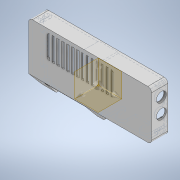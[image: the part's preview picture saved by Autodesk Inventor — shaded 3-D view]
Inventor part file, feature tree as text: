
AUTODESK INVENTOR PART (.ipt)
format: ipt  version: 2021 (Build 250183000, 183)  size: 576,512 bytes
history: native  units: mm
features: sketch x23, extrude x22, chamfer x6, fillet x5, hole x1
ambient origin geometry x8: Origin, YZ Plane, XZ Plane, XY Plane, X Axis, Y Axis, Z Axis, Center Point
bodies: Solid1 (feature_tree)
feature tree (57):
  extrude  "Extrusion1"  Depth=100.0mm
  extrude  "Extrusion3"  Depth=50.0mm
  extrude  "Extrusion4"  Depth=12.5mm
  extrude  "Extrusion12"  Depth=3.0mm TaperAngle=0.0deg
  extrude  "Extrusion13"  Depth=3.0mm TaperAngle=0.0deg
  fillet  "Fillet3"  Radius=2.0mm
  extrude  "Extrusion15"  Depth=2.0mm
  extrude  "Extrusion20"  Depth=1.2mm
  extrude  "Extrusion21"  Depth=12.0mm TaperAngle=0.0deg
  extrude  "Extrusion22"  Depth=2.0mm
  extrude  "Extrusion23"  Depth=3.0mm
  extrude  "Extrusion26"  Depth=4.4mm TaperAngle=0.0deg
  hole  "Hole2"  [1 undecoded]
  chamfer  "Chamfer3"  Distance=12.0mm
  chamfer  "Chamfer4"  Distance=12.0mm
  chamfer  "Chamfer5"  Distance=2.0mm
  chamfer  "Chamfer6"  Distance=2.0mm
  chamfer  "Chamfer7"  Distance=3.0mm
  extrude  "Extrusion27"  Depth=3.0mm
  fillet  "Fillet4"  Radius=50.0mm
  extrude  "Extrusion28"  Depth=0.5mm
  extrude  "Extrusion29"  Depth=15.0mm
  extrude  "Extrusion30"  Depth=3.0mm
  fillet  "Fillet5"  Radius=3.0mm
  extrude  "Extrusion34"  Depth=0.5mm
  extrude  "Extrusion35"  Depth=0.5mm
  extrude  "Extrusion36"  Depth=0.5mm
  extrude  "Extrusion37"  Depth=0.5mm
  fillet  "Fillet6"  Radius=4.8mm
  extrude  "Extrusion38"  Depth=0.5mm
  extrude  "Extrusion39"  Depth=0.5mm
  chamfer  "Chamfer8"  Distance=5.0mm
  extrude  "Extrusion40"  Depth=2.0mm TaperAngle=45.0deg
  fillet  "Fillet7"  Radius=1.0mm
  sketch  "Sketch1"  dims[d0=52.0mm d1=100.0mm]
  sketch  "Sketch4"  dims[d2=26.0mm d3=50.0mm]
  sketch  "Sketch5"  dims[d4=1.2mm d5=0.0mm d35=12.5mm]
  sketch  "Sketch13"  dims[d36=63.1mm d37=3.0mm d38=0.0mm]
  sketch  "Sketch14"  dims[d39=50.673mm d40=3.0mm d41=0.0mm d79=2.0mm]
  sketch  "Sketch16"  dims[d80=2.0mm d81=2.0mm]
  sketch  "Sketch21"  dims[d82=1.2mm d83=44.0mm]
  sketch  "Sketch22"  dims[d84=59.0mm d85=12.0mm d86=0.0mm]
  sketch  "Sketch23"  dims[d87=2.0mm d88=12.6mm]
  sketch  "Sketch24"  dims[d89=12.0mm d90=0.0mm d91=3.0mm]
  sketch  "Sketch27"  dims[d95=33.8mm d96=4.4mm d97=0.0mm]
  sketch  "Sketch28"  dims[d117=2.0mm d118=2.0mm d119=12.0mm d120=0.0mm d121=12.0mm d122=0.0mm]
  sketch  "Sketch29"  dims[d123=70.0mm]
  sketch  "Sketch30"  dims[d124=89.0mm]
  sketch  "Sketch31"  dims[d125=8.0mm]
  sketch  "Sketch32"  dims[d126=8.0mm d127=2.0mm d128=0.0mm]
  sketch  "Sketch36"  dims[d129=8.0mm]
  sketch  "Sketch37"  dims[d130=10.0mm]
  sketch  "Sketch38"  dims[d131=12.0mm]
  sketch  "Sketch39"  dims[d132=8.0mm]
  sketch  "Sketch40"  dims[d133=8.0mm]
  sketch  "Sketch41"  dims[d134=8.0mm d135=2.0mm d136=0.0mm]
  sketch  "Sketch43"  dims[d144=3.0mm d145=3.0mm d146=3.0mm d147=50.0mm d148=97.0mm d149=15.0mm d150=3.0mm d151=3.0mm d152=97.0mm d153=49.0mm d154=4.8mm d155=4.8mm d156=4.8mm d157=4.8mm d158=4.8mm d159=5.0mm d160=0.0mm d161=2.0mm d162=6.0mm d163=4.0mm d164=2.0mm d165=90.0deg d166=4.0mm d167=20.594885mm d168=2.0mm d169=2.0mm d170=45.0deg d171=1.0mm d172=2.0mm d173=45.0deg d174=2.0mm d175=2.0mm d176=45.0deg d177=2.0mm d178=2.0mm d179=45.0deg d180=0.8mm d181=2.0mm d182=45.0deg d184=68.0mm d189=2.0mm d190=0.0mm d191=2.0mm d192=2.0mm d193=24.0mm d194=2.0mm d195=0.0mm d196=36.5mm d197=46.5mm d198=3.5mm d199=2.0mm d200=0.0mm d201=12.5mm d202=23.0mm d203=3.5mm d204=2.0mm d205=0.0mm d206=1.0mm d217=7.6mm d218=10.0mm d219=46.4mm d220=20.0mm d221=0.0mm d222=22.68928mm d223=67.0mm d224=0.0mm d225=1.2mm d226=0.0mm d227=1.2mm d228=0.0mm d229=3.0mm d230=12.3mm d231=33.2mm d232=1.0mm d233=10.0mm d234=1.2mm d235=0.0mm d236=1.2mm d237=5.0mm d238=20.0mm d239=1.5mm d240=0.0mm d241=1.5mm d242=2.0mm d243=45.0deg d245=2.711255mm d246=12.0mm d247=33.2mm d248=3.0mm d249=0.0mm d251=2.0mm d67=0.5mm d68=0.872665mm d69=0.5mm d70=0.872665mm d71=0.5mm d72=0.872665mm d73=0.5mm d74=0.872665mm d75=0.872665mm d76=0.5mm d77=0.872665mm d208=0.5mm d209=0.872665mm d210=0.5mm d211=0.872665mm]
note: 1 required parameter value undecoded (feature->parameter linkage not recoverable at this tier; creation-order binding heuristic only, values carry confidence <= 0.55)
